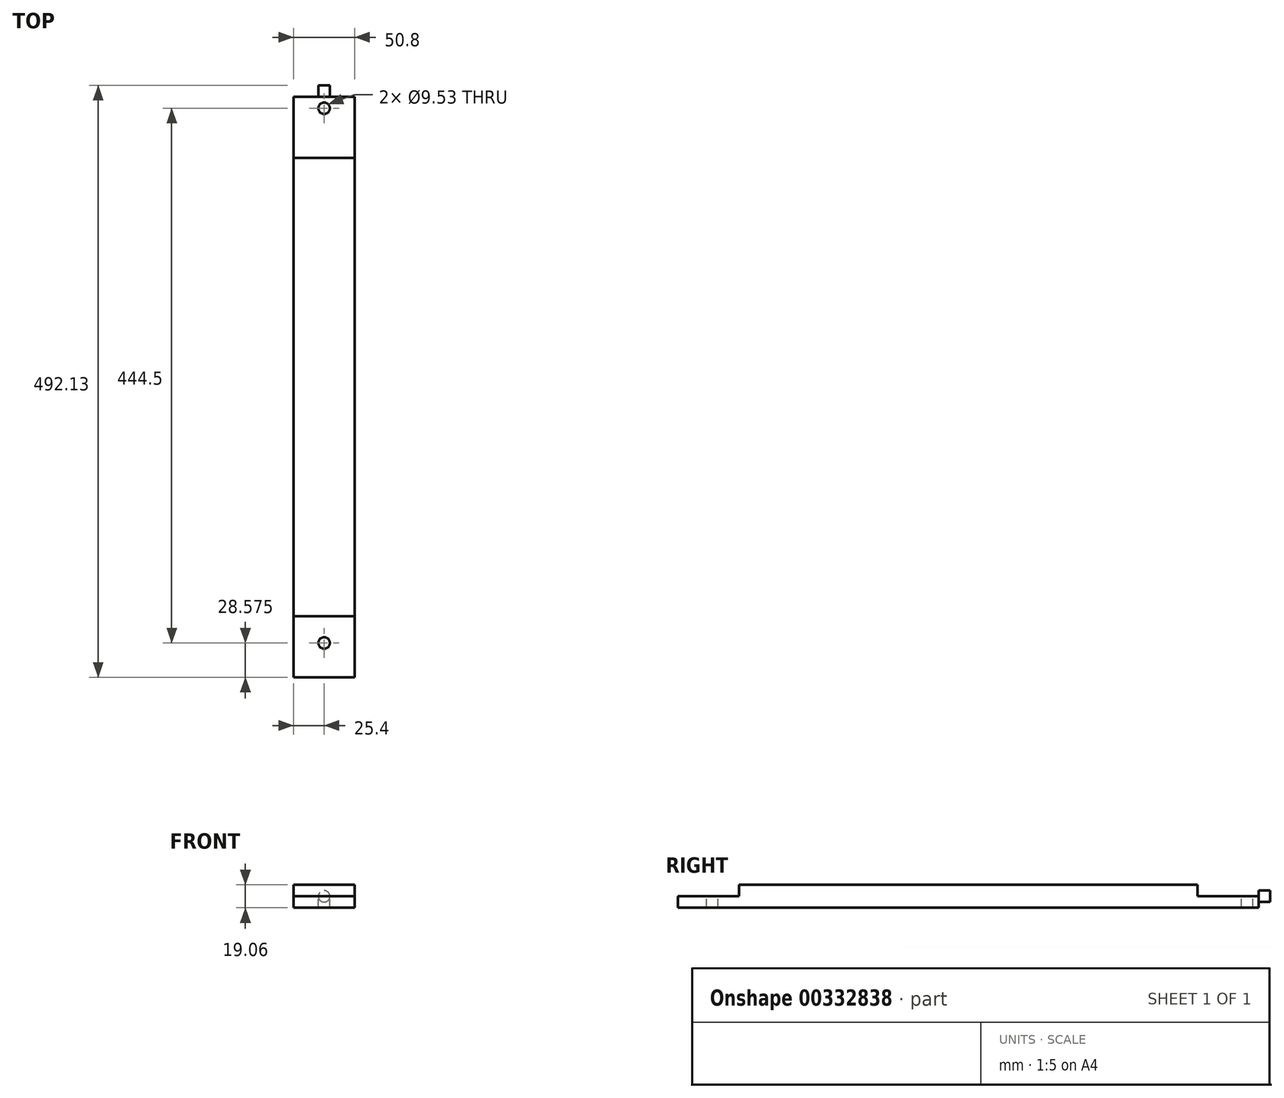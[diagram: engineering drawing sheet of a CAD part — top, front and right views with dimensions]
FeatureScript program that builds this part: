
annotation { "Feature Type Name" : "Feature", "Feature Type Description" : "" }
export const myFeature = defineFeature(function(context is Context, id is Id, definition is map)
    precondition{}
    {
        {
            var Q0;
            Q0=qCreatedBy(makeId("Right.planeOp"),FACE);
            var sketch = newSketch(context, id + "F0", { "sketchPlane" : qUnion([Q0])});
            skLineSegment(sketch, "E0", {"start": v(482.6, -9.52) * mm, "end": v(0, -9.52) * mm});
            skLineSegment(sketch, "E1.bottom", {"start": v(482.6, 9.53) * mm, "end": v(482.6, 0) * mm});
            skLineSegment(sketch, "E1.top", {"start": v(431.8, 9.53) * mm, "end": v(431.8, 0) * mm});
            skLineSegment(sketch, "E1.right", {"start": v(482.6, 0) * mm, "end": v(431.8, 0) * mm});
            skLineSegment(sketch, "E2.top", {"start": v(0, 9.53) * mm, "end": v(0, 0) * mm});
            skLineSegment(sketch, "E2.right", {"start": v(50.8, 0) * mm, "end": v(0, 0) * mm});
            skLineSegment(sketch, "E3", {"start": v(50.8, 0) * mm, "end": v(50.8, 9.53) * mm});
            skLineSegment(sketch, "E4.trimOffspring", {"start": v(50.8, 9.53) * mm, "end": v(431.8, 9.53) * mm});
            skLineSegment(sketch, "E5", {"start": v(0, 0) * mm, "end": v(0, -9.52) * mm});
            skLineSegment(sketch, "E6", {"start": v(482.6, 0) * mm, "end": v(482.6, -9.52) * mm});
            skSolve(sketch);
        }
        {
            var Q0;
            Q0=qSketchRegion(id+"F0",true);
            extrude(context, id + "F1", {"entities" : qUnion([Q0]), "endBound" : BoundingType.SYMMETRIC, "depth" : 50.8 * mm});
        }
        {
            var Q0;
            Q0=qCreatedBy(makeId("Top.planeOp"),FACE);
            var sketch = newSketch(context, id + "F2", { "sketchPlane" : qUnion([Q0])});
            skCircle(sketch, "E7", {"center": v(0, 28.58) * mm, "radius": 4.76 * mm});
            skCircle(sketch, "E8", {"center": v(0, 473.07) * mm, "radius": 4.76 * mm});
            skSolve(sketch);
        }
        {
            var Q0;
            Q0=qSketchRegion(id+"F2",true);
            extrude(context, id + "F3", {"entities" : qUnion([Q0]), "operationType" : NewBodyOperationType.REMOVE, "oppositeDirection" : true, "depth" : 25.4 * mm});
        }
        {
            var Q0;
            Q0=qCreatedBy(makeId("Front.planeOp"),FACE);
            cPlane(context, id + "F4", {"entities" : qUnion([Q0]), "cplaneType" : CPlaneType.OFFSET, "offset" : 482.6 * mm, "oppositeDirection" : true, "width" : 152.4 * mm, "height" : 152.4 * mm});
        }
        {
            var Q0;
            Q0=qCreatedBy(id+"F4.planeOp",FACE);
            var sketch = newSketch(context, id + "F5", { "sketchPlane" : qUnion([Q0])});
            skCircle(sketch, "E9", {"center": v(0, 0) * mm, "radius": 4.76 * mm});
            skSolve(sketch);
        }
        {
            var Q0;
            Q0=qSketchRegion(id+"F5",true);
            extrude(context, id + "F6", {"entities" : qUnion([Q0]), "operationType" : NewBodyOperationType.ADD, "oppositeDirection" : true, "depth" : 9.52 * mm});
        }
    });
